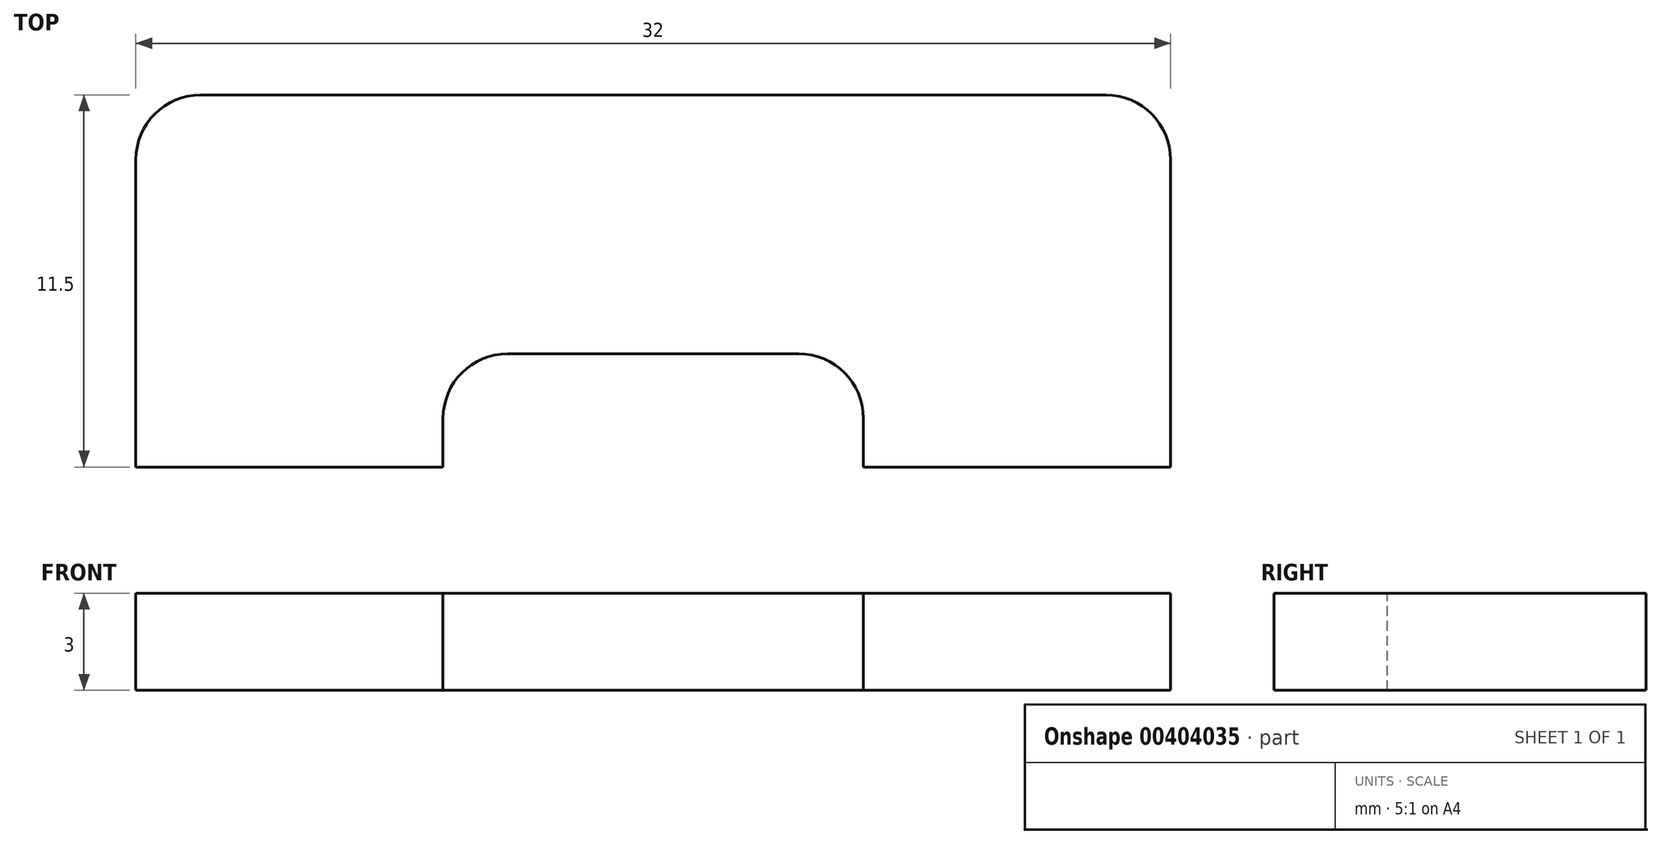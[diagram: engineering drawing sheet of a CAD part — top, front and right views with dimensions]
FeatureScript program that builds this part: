
annotation { "Feature Type Name" : "Feature", "Feature Type Description" : "" }
export const myFeature = defineFeature(function(context is Context, id is Id, definition is map)
    precondition{}
    {
        {
            var Q0;
            Q0=qCreatedBy(makeId("Top.planeOp"),FACE);
            var sketch = newSketch(context, id + "F0", { "sketchPlane" : qUnion([Q0])});
            skLineSegment(sketch, "E0.bottom", {"start": v(-16, 11.5) * mm, "end": v(16, 11.5) * mm});
            skLineSegment(sketch, "E0.top", {"start": v(-16, 0) * mm, "end": v(16, 0) * mm});
            skLineSegment(sketch, "E0.left", {"start": v(-16, 11.5) * mm, "end": v(-16, 0) * mm});
            skLineSegment(sketch, "E0.right", {"start": v(16, 11.5) * mm, "end": v(16, 0) * mm});
            skSolve(sketch);
        }
        {
            var Q0;
            Q0 = qSketchRegion(id + "F0", true);
            extrude(context, id + "F1", {"entities" : qUnion([Q0]), "depth" : 3 * mm});
        }
        {
            var Q0;
            Q0=makeQuery(id+"F1.opExtrude","SWEPT_EDGE",EDGE,{"disambiguationData":[OSD([sQuery(id+"F0.wireOp",EDGE,"E0.bottom"),sQuery(id+"F0.wireOp",EDGE,"E0.left")])]});
            var Q1;
            Q1=makeQuery(id+"F1.opExtrude","SWEPT_EDGE",EDGE,{"disambiguationData":[OSD([sQuery(id+"F0.wireOp",EDGE,"E0.bottom"),sQuery(id+"F0.wireOp",EDGE,"E0.right")])]});
            fillet(context, id + "F2", {"entities" : qUnion([Q0, Q1]), "radius" : 2 * mm, "tangentPropagation" : true, "allowEdgeOverflow" : false});
        }
        {
            var Q0;
            Q0=makeQuery(id+"F1.opExtrude","CAP_FACE",FACE,{"disambiguationData":[OSD([sQuery(id+"F0.wireOp",EDGE,"E0.bottom"),sQuery(id+"F0.wireOp",EDGE,"E0.top"),sQuery(id+"F0.wireOp",EDGE,"E0.left"),sQuery(id+"F0.wireOp",EDGE,"E0.right")])],"isStart":false});
            var sketch = newSketch(context, id + "F3", { "sketchPlane" : qUnion([Q0])});
            skLineSegment(sketch, "E1.bottom", {"start": v(-6.5, 3.5) * mm, "end": v(6.5, 3.5) * mm});
            skLineSegment(sketch, "E1.top", {"start": v(-6.5, 0) * mm, "end": v(6.5, 0) * mm});
            skLineSegment(sketch, "E1.left", {"start": v(-6.5, 3.5) * mm, "end": v(-6.5, 0) * mm});
            skLineSegment(sketch, "E1.right", {"start": v(6.5, 3.5) * mm, "end": v(6.5, 0) * mm});
            skSolve(sketch);
        }
        {
            var Q0;
            Q0 = qSketchRegion(id + "F3", true);
            extrude(context, id + "F4", {"entities" : qUnion([Q0]), "operationType" : NewBodyOperationType.REMOVE, "endBound" : BoundingType.THROUGH_ALL, "oppositeDirection" : true, "depth" : 25 * mm});
        }
        {
            var Q0;
            Q0=makeQuery(id+"F4.boolean.opBoolean","COPY",EDGE,{"derivedFrom":makeQuery(id+"F4.opExtrude","SWEPT_EDGE",EDGE,{"disambiguationData":[OSD([sQuery(id+"F3.wireOp",EDGE,"E1.bottom"),sQuery(id+"F3.wireOp",EDGE,"E1.left")])]})});
            var Q1;
            Q1=makeQuery(id+"F4.boolean.opBoolean","COPY",EDGE,{"derivedFrom":makeQuery(id+"F4.opExtrude","SWEPT_EDGE",EDGE,{"disambiguationData":[OSD([sQuery(id+"F3.wireOp",EDGE,"E1.bottom"),sQuery(id+"F3.wireOp",EDGE,"E1.right")])]})});
            fillet(context, id + "F5", {"entities" : qUnion([Q0, Q1]), "radius" : 2 * mm, "tangentPropagation" : true, "allowEdgeOverflow" : false});
        }
    });
